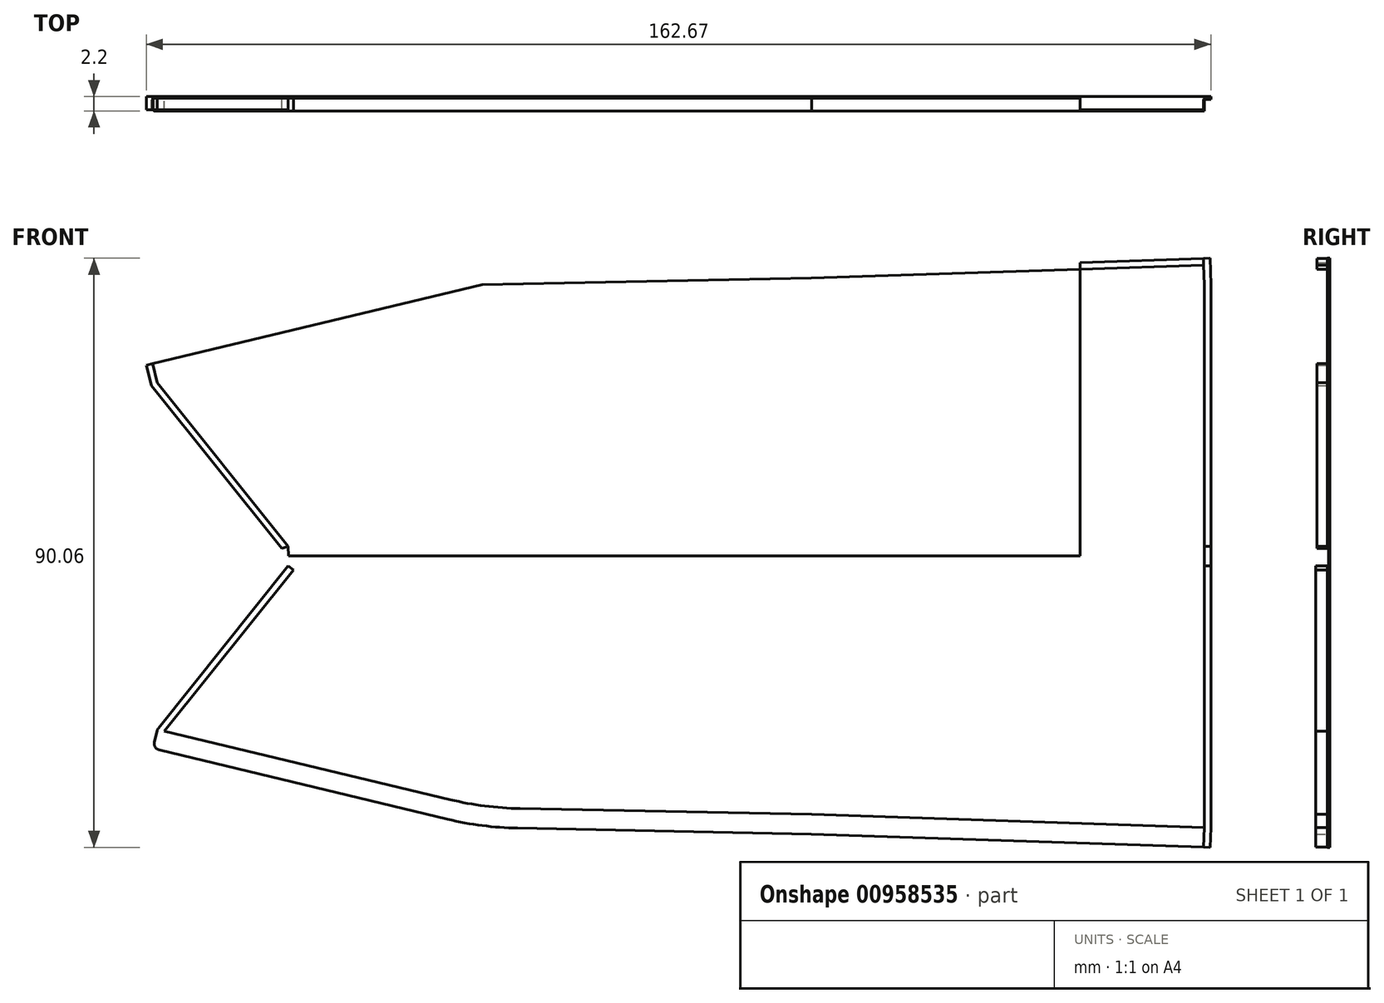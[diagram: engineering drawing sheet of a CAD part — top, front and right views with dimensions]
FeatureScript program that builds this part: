
annotation { "Feature Type Name" : "Feature", "Feature Type Description" : "" }
export const myFeature = defineFeature(function(context is Context, id is Id, definition is map)
    precondition{}
    {
        {
            var Q0;
            Q0=qCreatedBy(makeId("Front.planeOp"),FACE);
            var sketch = newSketch(context, id + "F0", { "sketchPlane" : qUnion([Q0])});
            skPoint(sketch, "E0", {"position": v(-81.84, 25) * mm});
            skPoint(sketch, "E1", {"position": v(78.16, 40) * mm});
            skPoint(sketch, "E2", {"position": v(-31.84, 37) * mm});
            skPoint(sketch, "E3", {"position": v(18.16, 38) * mm});
            skLineSegment(sketch, "E4", {"start": v(-81.84, 25) * mm, "end": v(-31.84, 37) * mm});
            skLineSegment(sketch, "E5", {"start": v(18.16, 38) * mm, "end": v(-31.84, 37) * mm});
            skLineSegment(sketch, "E6", {"start": v(-81.84, 25) * mm, "end": v(-61.84, 0) * mm});
            skLineSegment(sketch, "E7", {"start": v(78.16, 0) * mm, "end": v(78.16, 40) * mm});
            skLineSegment(sketch, "E8.0", {"start": v(18.08, 41) * mm, "end": v(78.06, 43) * mm});
            skLineSegment(sketch, "E8.1", {"start": v(18.08, 41) * mm, "end": v(-32.22, 40) * mm});
            skLineSegment(sketch, "E8.2", {"start": v(-82.54, 27.92) * mm, "end": v(-32.22, 40) * mm});
            skLineSegment(sketch, "E9", {"start": v(-81.84, 25) * mm, "end": v(-82.54, 27.92) * mm});
            skLineSegment(sketch, "E10", {"start": v(78.16, 40) * mm, "end": v(78.06, 43) * mm});
            skLineSegment(sketch, "E11", {"start": v(78.16, 0) * mm, "end": v(78.16, -1.5) * mm});
            skLineSegment(sketch, "E12", {"start": v(-61.81, -1.5) * mm, "end": v(-61.84, 0) * mm});
            skLineSegment(sketch, "E13.MirrorCS", {"start": v(-61.81, -1.5) * mm, "end": v(-61.84, -3) * mm});
            skLineSegment(sketch, "E14.MirrorCS", {"start": v(-81.84, -28) * mm, "end": v(-61.84, -3) * mm});
            skLineSegment(sketch, "E15.MirrorCS", {"start": v(-81.84, -28) * mm, "end": v(-82.54, -30.92) * mm});
            skLineSegment(sketch, "E16.MirrorCS", {"start": v(-82.54, -30.92) * mm, "end": v(-32.22, -43) * mm});
            skLineSegment(sketch, "E17.MirrorCS", {"start": v(-81.84, -28) * mm, "end": v(-31.84, -40) * mm});
            skLineSegment(sketch, "E18.MirrorCS", {"start": v(18.16, -41) * mm, "end": v(-31.84, -40) * mm});
            skLineSegment(sketch, "E19.MirrorCS", {"start": v(18.08, -44) * mm, "end": v(-32.22, -43) * mm});
            skLineSegment(sketch, "E20.MirrorCS", {"start": v(18.16, -41) * mm, "end": v(78.16, -43) * mm});
            skLineSegment(sketch, "E21.MirrorCS", {"start": v(18.08, -44) * mm, "end": v(78.06, -46) * mm});
            skLineSegment(sketch, "E22.MirrorCS", {"start": v(78.16, -43) * mm, "end": v(78.06, -46) * mm});
            skLineSegment(sketch, "E23.MirrorCS", {"start": v(78.16, -3) * mm, "end": v(78.16, -43) * mm});
            skLineSegment(sketch, "E24.MirrorCS", {"start": v(78.16, -3) * mm, "end": v(78.16, -1.5) * mm});
            skLineSegment(sketch, "E25.0", {"start": v(18.06, 42) * mm, "end": v(78.03, 44) * mm});
            skLineSegment(sketch, "E25.1", {"start": v(18.06, 42) * mm, "end": v(-32.35, 41) * mm});
            skLineSegment(sketch, "E25.2", {"start": v(-82.77, 28.89) * mm, "end": v(-32.35, 41) * mm});
            skLineSegment(sketch, "E26", {"start": v(78.06, 43) * mm, "end": v(78.03, 44) * mm});
            skLineSegment(sketch, "E27.0", {"start": v(-83.51, 27.68) * mm, "end": v(-83.74, 28.66) * mm});
            skLineSegment(sketch, "E27.1", {"start": v(-82.76, 24.55) * mm, "end": v(-83.51, 27.68) * mm});
            skLineSegment(sketch, "E27.2", {"start": v(-82.76, 24.55) * mm, "end": v(-62.83, -0.36) * mm});
            skLineSegment(sketch, "E28", {"start": v(-83.74, 28.66) * mm, "end": v(-82.77, 28.89) * mm});
            skLineSegment(sketch, "E29", {"start": v(-82.54, 27.92) * mm, "end": v(-83.51, 27.68) * mm});
            skLineSegment(sketch, "E30.0", {"start": v(79.06, 43.03) * mm, "end": v(79.03, 44.03) * mm});
            skLineSegment(sketch, "E30.1", {"start": v(79.16, 40.02) * mm, "end": v(79.06, 43.03) * mm});
            skLineSegment(sketch, "E30.2", {"start": v(79.16, 0) * mm, "end": v(79.16, 40.02) * mm});
            skLineSegment(sketch, "E30.3", {"start": v(79.16, 0) * mm, "end": v(79.16, -1.5) * mm});
            skLineSegment(sketch, "E31", {"start": v(79.03, 44.03) * mm, "end": v(78.03, 44) * mm});
            skLineSegment(sketch, "E32", {"start": v(79.16, 0) * mm, "end": v(78.16, 0) * mm});
            skLineSegment(sketch, "E33.0", {"start": v(79.16, -43.02) * mm, "end": v(79.06, -46.03) * mm});
            skLineSegment(sketch, "E33.1", {"start": v(79.16, -3) * mm, "end": v(79.16, -43.02) * mm});
            skLineSegment(sketch, "E34", {"start": v(78.06, -46) * mm, "end": v(79.06, -46.03) * mm});
            skLineSegment(sketch, "E35", {"start": v(78.16, -3) * mm, "end": v(79.16, -3) * mm});
            skLineSegment(sketch, "E36", {"start": v(79.16, -3) * mm, "end": v(79.16, -1.5) * mm});
            skLineSegment(sketch, "E37.0", {"start": v(-81.06, -28.62) * mm, "end": v(-61.06, -3.62) * mm});
            skLineSegment(sketch, "E38", {"start": v(-61.06, -3.62) * mm, "end": v(-61.84, -3) * mm});
            skLineSegment(sketch, "E39", {"start": v(-62.83, -0.36) * mm, "end": v(-61.84, 0) * mm});
            skLineSegment(sketch, "E40", {"start": v(59.16, -1.5) * mm, "end": v(59.16, 39.37) * mm});
            skLineSegment(sketch, "E41", {"start": v(59.16, -1.5) * mm, "end": v(-61.81, -1.5) * mm});
            skLineSegment(sketch, "E42", {"start": v(59.16, 39.37) * mm, "end": v(18.16, 38) * mm});
            skLineSegment(sketch, "E43", {"start": v(59.16, 39.37) * mm, "end": v(59.16, 43.37) * mm});
            skSolve(sketch);
        }
        {
            var Q0;
            Q0=makeQuery(id+"F0.imprint","IMPRINT",FACE,{"disambiguationData":[TD([[makeQuery(id+"F0.imprint","IMPRINT",EDGE,{"derivedFrom":sQuery(id+"F0.wireOp",EDGE,"E4")}),-1.0]])]});
            var Q1;
            Q1=makeQuery(id+"F0.imprint","IMPRINT",FACE,{"disambiguationData":[TD([[makeQuery(id+"F0.imprint","IMPRINT",EDGE,{"derivedFrom":sQuery(id+"F0.wireOp",EDGE,"bDBm0fu8-Yuij-XiWd-KpGw-tzxEyUS1P9rg")}),1.0]])]});
            var Q2;
            Q2=makeQuery(id+"F0.imprint","IMPRINT",FACE,{"disambiguationData":[TD([[makeQuery(id+"F0.imprint","IMPRINT",EDGE,{"derivedFrom":sQuery(id+"F0.wireOp",EDGE,"E4")}),1.0]])]});
            var Q3;
            Q3=makeQuery(id+"F0.imprint","IMPRINT",FACE,{"disambiguationData":[TD([[makeQuery(id+"F0.imprint","IMPRINT",EDGE,{"derivedFrom":sQuery(id+"F0.wireOp",EDGE,"E11")}),1.0]])]});
            extrude(context, id + "F1", {"entities" : qUnion([Q0, Q1, Q2, Q3]), "depth" : 0.2 * mm, "offsetDistance" : 25 * mm});
        }
        {
            var Q0;
            Q0=makeQuery(id+"F0.imprint","IMPRINT",FACE,{"disambiguationData":[TD([[makeQuery(id+"F0.imprint","IMPRINT",EDGE,{"derivedFrom":sQuery(id+"F0.wireOp",EDGE,"E8.0")}),1.0]])]});
            var Q1;
            Q1=makeQuery(id+"F0.imprint","IMPRINT",FACE,{"disambiguationData":[TD([[makeQuery(id+"F0.imprint","IMPRINT",EDGE,{"derivedFrom":sQuery(id+"F0.wireOp",EDGE,"E6")}),-1.0]])]});
            extrude(context, id + "F2", {"entities" : qUnion([Q0, Q1]), "operationType" : NewBodyOperationType.ADD, "depth" : 2 * mm, "offsetDistance" : 25 * mm});
        }
        {
            var Q0;
            Q0=makeQuery(id+"F0.imprint","IMPRINT",FACE,{"disambiguationData":[TD([[makeQuery(id+"F0.imprint","IMPRINT",EDGE,{"derivedFrom":sQuery(id+"F0.wireOp",EDGE,"E15.MirrorCS")}),1.0]])]});
            var Q1;
            {var subQ0=sQuery(id+"F0.wireOp",EDGE,"E14.MirrorCS");Q1=makeQuery(id+"F0.imprint","IMPRINT",FACE,{"disambiguationData":[TD([[makeQuery(id+"F0.imprint","IMPRINT",EDGE,{"derivedFrom":subQ0}),-1.0]])]});}
            extrude(context, id + "F3", {"entities" : qUnion([Q0, Q1]), "operationType" : NewBodyOperationType.ADD, "depth" : 2.2 * mm, "offsetDistance" : 25 * mm});
        }
        {
            var Q0;
            Q0=makeQuery(id+"F2.opExtrude","SWEPT_EDGE",EDGE,{"disambiguationData":[OSD([sQuery(id+"F0.wireOp",EDGE,"E8.1"),sQuery(id+"F0.wireOp",EDGE,"E8.2")])]});
            var Q1;
            Q1=makeQuery(id+"F2.opExtrude","SWEPT_EDGE",EDGE,{"disambiguationData":[OSD([sQuery(id+"F0.wireOp",EDGE,"E25.1"),sQuery(id+"F0.wireOp",EDGE,"E25.2")])]});
            var Q2;
            Q2=makeQuery(id+"F3.opExtrude","SWEPT_EDGE",EDGE,{"disambiguationData":[OSD([sQuery(id+"F0.wireOp",EDGE,"E17.MirrorCS"),sQuery(id+"F0.wireOp",EDGE,"E18.MirrorCS")])]});
            var Q3;
            Q3=makeQuery(id+"F3.opExtrude","SWEPT_EDGE",EDGE,{"disambiguationData":[OSD([sQuery(id+"F0.wireOp",EDGE,"E16.MirrorCS"),sQuery(id+"F0.wireOp",EDGE,"E19.MirrorCS")])]});
            fillet(context, id + "F4", {"entities" : qUnion([Q0, Q1, Q2, Q3]), "radius" : 50 * mm, "tangentPropagation" : true, "allowEdgeOverflow" : false});
        }
        {
            var Q0;
            Q0=makeQuery(id+"F2.opExtrude","SWEPT_EDGE",EDGE,{"disambiguationData":[OSD([sQuery(id+"F0.wireOp",EDGE,"E27.0"),sQuery(id+"F0.wireOp",EDGE,"E28")])]});
            var Q1;
            Q1=makeQuery(id+"F2.opExtrude","SWEPT_EDGE",EDGE,{"disambiguationData":[OSD([sQuery(id+"F0.wireOp",EDGE,"E27.1"),sQuery(id+"F0.wireOp",EDGE,"E27.2")])]});
            var Q2;
            Q2=makeQuery(id+"F2.opExtrude","SWEPT_EDGE",EDGE,{"disambiguationData":[OSD([sQuery(id+"F0.wireOp",EDGE,"E8.2"),sQuery(id+"F0.wireOp",EDGE,"E9"),sQuery(id+"F0.wireOp",EDGE,"E29")])]});
            var Q3;
            Q3=makeQuery(id+"F2.opExtrude","SWEPT_EDGE",EDGE,{"disambiguationData":[OSD([sQuery(id+"F0.wireOp",EDGE,"E4"),sQuery(id+"F0.wireOp",EDGE,"E6"),sQuery(id+"F0.wireOp",EDGE,"E9")])]});
            var Q4;
            Q4=makeQuery(id+"F3.opExtrude","SWEPT_EDGE",EDGE,{"disambiguationData":[OSD([sQuery(id+"F0.wireOp",EDGE,"E15.MirrorCS"),sQuery(id+"F0.wireOp",EDGE,"E16.MirrorCS")])]});
            var Q5;
            Q5=makeQuery(id+"F3.opExtrude","SWEPT_EDGE",EDGE,{"disambiguationData":[OSD([sQuery(id+"F0.wireOp",EDGE,"E14.MirrorCS"),sQuery(id+"F0.wireOp",EDGE,"E15.MirrorCS"),sQuery(id+"F0.wireOp",EDGE,"E17.MirrorCS")])]});
            fillet(context, id + "F5", {"entities" : qUnion([Q0, Q1, Q2, Q3, Q4, Q5]), "radius" : 1 * mm, "tangentPropagation" : true, "allowEdgeOverflow" : false});
        }
        {
            var Q0;
            Q0=makeQuery(id+"F0.imprint","IMPRINT",FACE,{"disambiguationData":[TD([[makeQuery(id+"F0.imprint","IMPRINT",EDGE,{"derivedFrom":sQuery(id+"F0.wireOp",EDGE,"E7")}),-1.0]])]});
            var Q1;
            Q1=makeQuery(id+"F0.imprint","IMPRINT",FACE,{"disambiguationData":[TD([[makeQuery(id+"F0.imprint","IMPRINT",EDGE,{"derivedFrom":sQuery(id+"F0.wireOp",EDGE,"E22.MirrorCS")}),1.0]])]});
            extrude(context, id + "F6", {"entities" : qUnion([Q0, Q1]), "operationType" : NewBodyOperationType.ADD, "depth" : 0.4 * mm, "offsetDistance" : 25 * mm});
        }
    });
